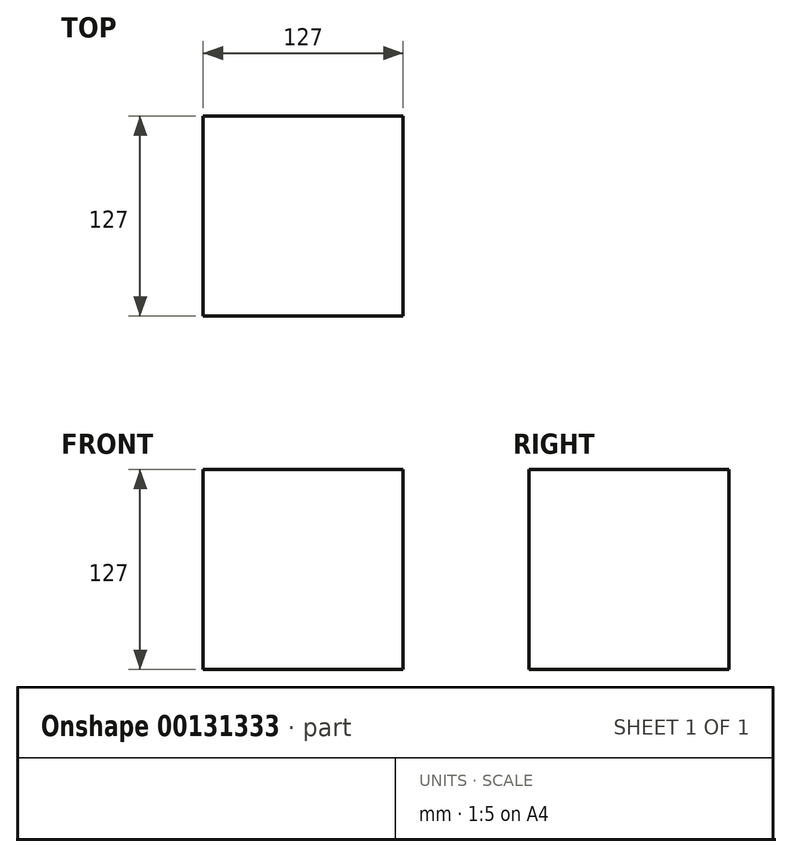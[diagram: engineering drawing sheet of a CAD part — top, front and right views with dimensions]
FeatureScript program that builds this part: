
annotation { "Feature Type Name" : "Feature", "Feature Type Description" : "" }
export const myFeature = defineFeature(function(context is Context, id is Id, definition is map)
    precondition{}
    {
        {
            var Q0;
            Q0=qCreatedBy(makeId("Front.planeOp"),FACE);
            var sketch = newSketch(context, id + "F0", { "sketchPlane" : qUnion([Q0])});
            skLineSegment(sketch, "E0.bottom", {"start": v(63.5, 63.5) * mm, "end": v(-63.5, 63.5) * mm});
            skLineSegment(sketch, "E0.top", {"start": v(63.5, -63.5) * mm, "end": v(-63.5, -63.5) * mm});
            skLineSegment(sketch, "E0.left", {"start": v(63.5, 63.5) * mm, "end": v(63.5, -63.5) * mm});
            skLineSegment(sketch, "E0.right", {"start": v(-63.5, 63.5) * mm, "end": v(-63.5, -63.5) * mm});
            skPoint(sketch, "E0.middle", {"position": v(0, 0) * mm});
            skSolve(sketch);
        }
        {
            var Q0;
            Q0 = qSketchRegion(id + "F0", true);
            extrude(context, id + "F1", {"entities" : qUnion([Q0]), "depth" : 127 * mm});
        }
    });
